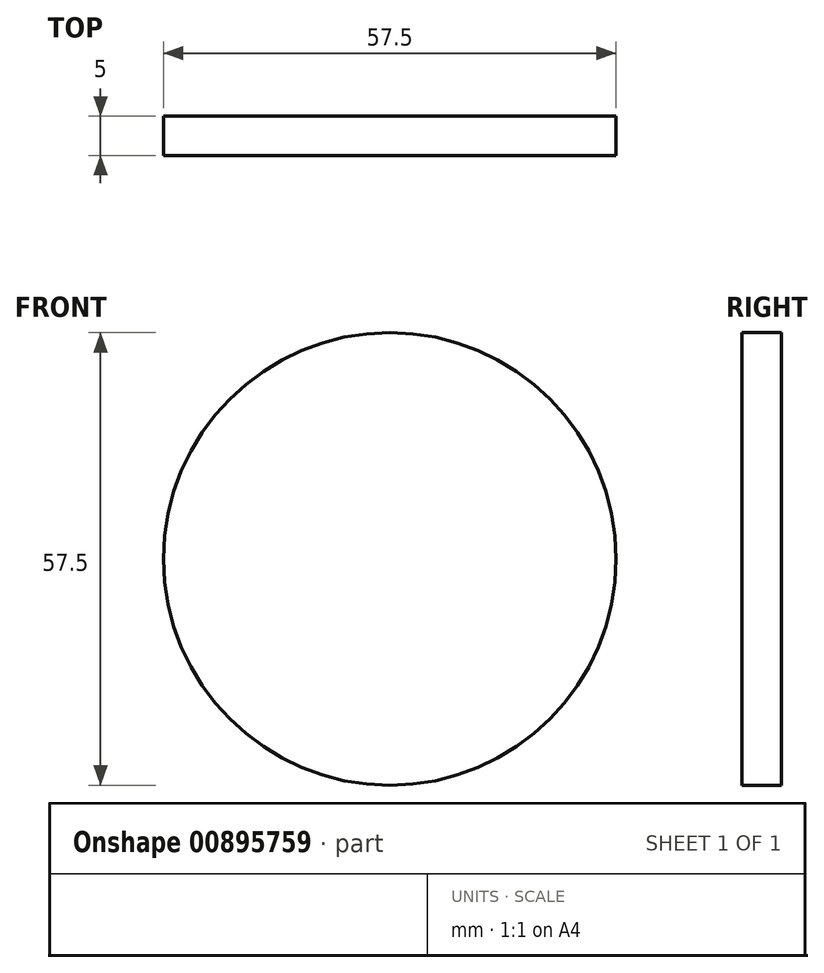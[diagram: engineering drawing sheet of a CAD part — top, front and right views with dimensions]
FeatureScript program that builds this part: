
annotation { "Feature Type Name" : "Feature", "Feature Type Description" : "" }
export const myFeature = defineFeature(function(context is Context, id is Id, definition is map)
    precondition{}
    {
        {
            var Q0;
            Q0=qCreatedBy(makeId("Front.planeOp"),FACE);
            var sketch = newSketch(context, id + "F0", { "sketchPlane" : qUnion([Q0])});
            skCircle(sketch, "E0", {"center": v(0, 0) * mm, "radius": 28.75 * mm});
            skSolve(sketch);
        }
        {
            var Q0;
            Q0=makeQuery(id+"F0.imprint","IMPRINT",FACE,{"disambiguationData":[TD([[makeQuery(id+"F0.imprint","IMPRINT",EDGE,{"derivedFrom":sQuery(id+"F0.wireOp",EDGE,"E0")}),1.0]])]});
            extrude(context, id + "F1", {"entities" : qUnion([Q0]), "offsetDistance" : 25 * mm, "depth" : 5 * mm});
        }
    });
